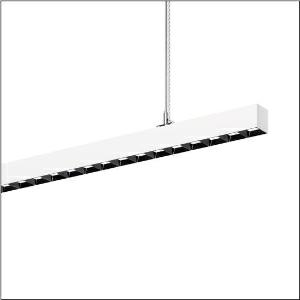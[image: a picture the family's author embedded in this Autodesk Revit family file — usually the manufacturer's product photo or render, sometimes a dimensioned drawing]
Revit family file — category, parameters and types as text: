
# Revit family: silica_r__21_51mx31tctdw_2edc
name_source: partatom
category: Lighting Fixtures
units: mm (PartAtom-declared; Revit-internal decimal feet)

## family parameters
Cut with Voids When Loaded = No
Host = Face
Light Source = No
Part Type = Normal
Room Calculation Point = No
Round Connector Dimension = Use Diameter
Shared = No

## types (1)
- --- (1 x LED, 15550 lm, 133.9 W, 6500K)
    Apparent Load = 134 VA
    CIE Flux Codes = 85 99 100 60 100
    Color Rendering = 80
    Color Temperature = 6500K
    Default Elevation = 1800 mm
    Description = Silica® 21, office luminaire, primary light control with darklight reflector, of PMMA, black, CAT 2 (L<= 3000cd/m²), light emission: direct/indirect distribution, primary light characteristic: symmetric, installation type: suspended mounting, LED, rated luminous flux: 15.550lm, luminous efficacy: 111lm/W, light colour: 8tw, colour temperature: 2700..6500K, control gear: ECG DALI, with terminal, 3+2-pole, max. 2.5mm², mains connection: 220..240V, AC, 50/60Hz, rated input power: 140.6W, luminaire housing, of aluminium, traffic white (RAL 9016), length: 3.004mm, width: 53mm, height: 53mm, protection rating (complete): IP20, insulation class (complete): insulation class I (protective earthing), certification: CE, permissible operating ambient temperature: 0..+35°C, standard: EN 50419, packaging unit: 1 piece
    Height = 53 mm
    Lamp = 1 x LED
    Lamp Light Flux = 15550 lm
    Lamp Power = 133.9 W
    Lamp count = 1
    Length = 3004 mm
    Luminous efficacy = 116 lm/W
    Manufacturer = Siteco
    ModVariant = No
    Model = 51MX31TCTDW
    Mounting Place = Ceiling
    Mounting Type = Pendant
    Number of Poles = 1
    OnlyDefault = Yes
    Power Factor = 1
    Product Name = Silica® 21
    Product group = office luminaire | ceiling pendant
    ProductGroupID = 902
    Protection Class = Protection class I
    Protection Degree = IP 20
    RLX_Detail_Level = 1
    RLX_Emergency_Light_Flux = 0 lm
    RLX_Emergency_Type = 0
    RLX_Emergency_Type_DB = No
    RlxData = <blob elided: 60593 chars, md5=dc4e67b7>
    Socket = socket
    Standby Power = 0 W
    System Light Flux = 15550 lm
    System Power = 134 W
    Type Comments = individual setting
    Type Image = l_1297801.jpg
    URL = http://relux.com
    VarID = @adj_071221
    Voltage = 0 V
    Weight = 0.00 kg
    Width = 53 mm

## geometry (parser evidence)
native form markers: Blend x4, Sweep x14
no freeform markers — native parametric forms only
